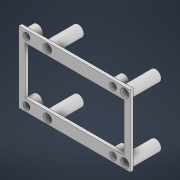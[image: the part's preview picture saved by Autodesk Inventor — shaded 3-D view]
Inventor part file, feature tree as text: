
AUTODESK INVENTOR PART (.ipt)
format: ipt  version: 2021 (Build 250183000, 183)  size: 422,400 bytes
history: native  units: mm
features: extrude x8, sketch x8
ambient origin geometry x8: Origin, YZ Plane, XZ Plane, XY Plane, X Axis, Y Axis, Z Axis, Center Point
bodies: Volumenkörper1 (feature_tree)
feature tree (16):
  extrude  "Extrusion1"  Depth=46.0mm
  extrude  "Extrusion2"  Depth=7.0mm
  extrude  "Extrusion3"  Depth=7.0mm
  extrude  "Extrusion4"  Depth=3.5mm
  extrude  "Extrusion5"  Depth=3.5mm
  extrude  "Extrusion6"  Depth=3.5mm
  extrude  "Extrusion7"  Depth=3.5mm
  extrude  "Extrusion8"  Depth=18.0mm TaperAngle=0.0deg
  sketch  "Skizze1"  dims[d0=57.0mm d1=46.0mm]
  sketch  "Skizze2"  dims[d2=2.0mm d3=0.0mm d4=7.0mm]
  sketch  "Skizze3"  dims[d5=7.0mm d6=7.0mm]
  sketch  "Skizze4"  dims[d7=7.0mm d8=3.5mm]
  sketch  "Skizze5"  dims[d9=3.5mm d10=3.5mm]
  sketch  "Skizze6"  dims[d11=3.5mm d12=3.5mm]
  sketch  "Skizze7"  dims[d13=3.5mm d14=3.5mm]
  sketch  "Skizze8"  dims[d15=3.5mm d16=18.0mm d17=0.0mm d18=5.5mm d19=5.5mm d20=5.5mm d21=5.5mm d22=3.5mm d23=3.5mm d24=3.5mm d25=3.5mm d26=3.5mm d27=3.5mm d28=3.5mm d29=3.5mm d30=4.0mm d31=0.0mm d32=3.2mm d33=3.2mm d34=3.2mm d35=3.2mm d36=4.0mm d37=0.0mm d38=15.0mm d39=0.0mm d40=4.5mm d41=4.5mm d42=4.5mm d43=4.5mm d44=39.0mm d45=39.0mm d46=19.5mm d47=19.5mm d48=19.5mm d49=19.5mm d50=56.0mm d51=5.0mm d53=7.0mm d54=3.5mm d55=5.0mm d56=7.0mm d57=5.0mm d58=3.5mm d59=7.0mm d60=3.5mm d61=11.0mm d62=7.0mm d63=3.5mm d64=11.0mm d65=5.0mm d66=0.0mm d67=6.0mm d68=0.0mm d69=4.0mm d70=7.5mm d71=4.0mm d72=7.5mm d73=6.0mm d74=0.0mm]
